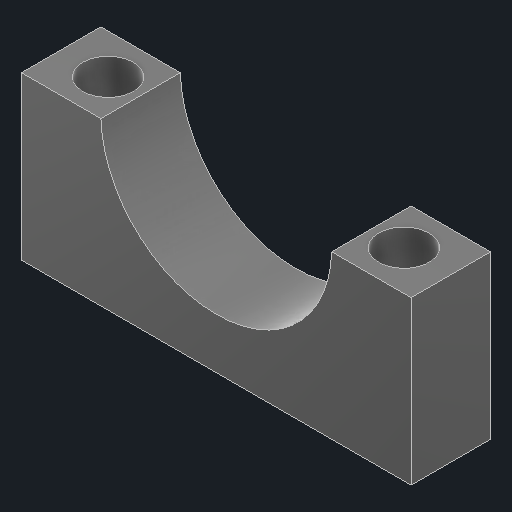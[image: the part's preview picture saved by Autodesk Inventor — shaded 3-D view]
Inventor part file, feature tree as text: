
AUTODESK INVENTOR PART (.ipt)
format: ipt  version: 2024.1 (Build 281209000, 209)  size: 187,392 bytes
history: native  units: mm
features: extrude x2
ambient origin geometry x8: Origin, YZ Plane, XZ Plane, XY Plane, X Axis, Y Axis, Z Axis, Center Point
bodies: Solid1 (feature_tree)
feature tree (2):
  extrude  "Extrusion1"  Depth=16.0mm
  extrude  "Extrusion2"  Depth=27.0mm
